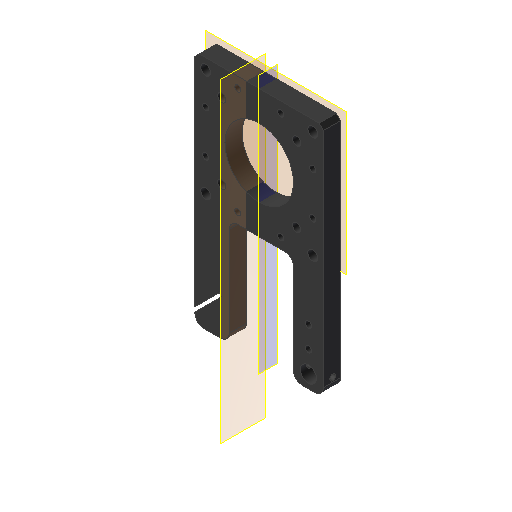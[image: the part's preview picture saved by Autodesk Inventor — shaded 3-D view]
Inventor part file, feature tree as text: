
AUTODESK INVENTOR PART (.ipt)
format: ipt  version: 2022 (Build 260153000, 153)  size: 271,360 bytes
history: native  units: mm
features: extrude x7, sketch x6, projected_geometry x5, other x4, plane x3, reference x2, fillet x1
ambient origin geometry x8: Origin, YZ Plane, XZ Plane, XY Plane, X Axis, Y Axis, Z Axis, Center Point
bodies: Solid1 (feature_tree)
feature tree (28):
  plane  "Work Plane1"
  extrude  "Extrusion1"  Depth=8.0mm TaperAngle=0.0deg
  extrude  "Extrusion2"  Depth=4.0mm
  fillet  "Fillet1"  Radius=4.0mm
  plane  "Work Plane2"
  extrude  "Extrusion7"  Depth=50.0mm
  extrude  "Extrusion10"  Depth=7.5mm
  extrude  "Extrusion11"  Depth=10.0mm
  extrude  "Extrusion12"  Depth=10.0mm
  extrude  "Extrusion13"  Depth=10.0mm
  plane  "Work Plane3"
  sketch  "Sketch1"  dims[d1=8.0mm d2=0.0mm d6=7.0mm d7=0.0mm]
  reference  "Reference1"
  reference  "Reference2"
  projected_geometry  "Projected Loop1"
  sketch  "Sketch8"  dims[d12=4.0mm d41=32.0mm d42=4.0mm d43=0.0mm]
  sketch  "Sketch11"  dims[d57=14.0mm d58=50.0mm]
  projected_geometry  "Projected Loop9"
  sketch  "Sketch12"  dims[d59=16.0mm d77=7.5mm]
  projected_geometry  "Projected Loop10"
  sketch  "Sketch13"  dims[d78=10.0mm d79=0.0mm d80=2.9mm]
  projected_geometry  "Projected Loop11"
  sketch  "Sketch14"  dims[d81=2.9mm d82=10.0mm d83=10.0mm d84=6.0mm d85=2.9mm d86=10.0mm d87=0.0mm d88=25.0mm d89=45.0deg d90=1.5mm d91=10.0mm d92=0.0mm d93=2.9mm d94=2.9mm d95=10.0mm d96=0.0mm]
  projected_geometry  "Projected Loop12"
  other  "Application_Fluorescence_Microscope_Infinity_cellstorm_v3.iam"
  other  "00_XY_stage-CHUO_SEIKI_LD-647-R1:1"
  other  "00_XY_stage-CHUO_SEIKI_LD-647-R1-Top:1"
  other  "00_Microscope_Objective:1"
